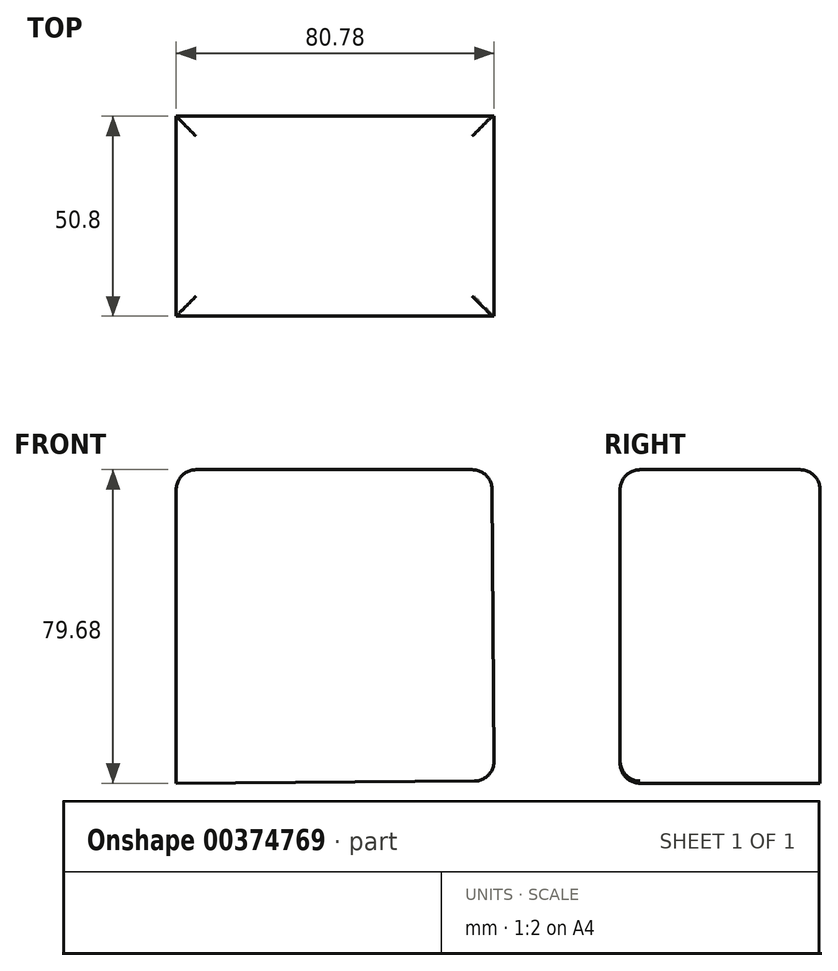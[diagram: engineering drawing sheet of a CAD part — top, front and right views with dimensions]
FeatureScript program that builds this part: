
annotation { "Feature Type Name" : "Feature", "Feature Type Description" : "" }
export const myFeature = defineFeature(function(context is Context, id is Id, definition is map)
    precondition{}
    {
        {
            var Q0;
            Q0=qCreatedBy(makeId("Front.planeOp"),FACE);
            var sketch = newSketch(context, id + "F0", { "sketchPlane" : qUnion([Q0])});
            skLineSegment(sketch, "E0", {"start": v(-36.76, 45.18) * mm, "end": v(43.48, 45.18) * mm});
            skLineSegment(sketch, "E1", {"start": v(43.48, 45.18) * mm, "end": v(44.06, -33.92) * mm});
            skLineSegment(sketch, "E2", {"start": v(44.06, -33.92) * mm, "end": v(-36.76, -34.5) * mm});
            skLineSegment(sketch, "E3", {"start": v(-36.76, -34.5) * mm, "end": v(-36.76, 45.18) * mm});
            skSolve(sketch);
        }
        {
            var Q0;
            Q0=makeQuery(id+"F0.imprint","IMPRINT",FACE,{"disambiguationData":[TD([[makeQuery(id+"F0.imprint","IMPRINT",EDGE,{"derivedFrom":sQuery(id+"F0.wireOp",EDGE,"E0")}),-1.0]])]});
            extrude(context, id + "F1", {"entities" : qUnion([Q0]), "depth" : 50.8 * mm});
        }
        {
            var Q0;
            Q0=makeQuery(id+"F1.opExtrude","SWEPT_EDGE",EDGE,{"disambiguationData":[OSD([sQuery(id+"F0.wireOp",EDGE,"E0"),sQuery(id+"F0.wireOp",EDGE,"E3")])]});
            var Q1;
            Q1=makeQuery(id+"F1.opExtrude","SWEPT_EDGE",EDGE,{"disambiguationData":[OSD([sQuery(id+"F0.wireOp",EDGE,"E0"),sQuery(id+"F0.wireOp",EDGE,"E1")])]});
            var Q2;
            Q2=makeQuery(id+"F1.opExtrude","CAP_EDGE",EDGE,{"disambiguationData":[OSD([sQuery(id+"F0.wireOp",EDGE,"E0")])],"isStart":false});
            var Q3;
            Q3=makeQuery(id+"F1.opExtrude","CAP_EDGE",EDGE,{"disambiguationData":[OSD([sQuery(id+"F0.wireOp",EDGE,"E0")])],"isStart":true});
            var Q4;
            Q4=makeQuery(id+"F1.opExtrude","SWEPT_EDGE",EDGE,{"disambiguationData":[OSD([sQuery(id+"F0.wireOp",EDGE,"E1"),sQuery(id+"F0.wireOp",EDGE,"E2")])]});
            var Q5;
            Q5=makeQuery(id+"F1.opExtrude","CAP_EDGE",EDGE,{"disambiguationData":[OSD([sQuery(id+"F0.wireOp",EDGE,"E2")])],"isStart":false});
            fillet(context, id + "F2", {"entities" : qUnion([Q0, Q1, Q2, Q3, Q4, Q5]), "radius" : 5.08 * mm, "tangentPropagation" : true, "allowEdgeOverflow" : false});
        }
    });
